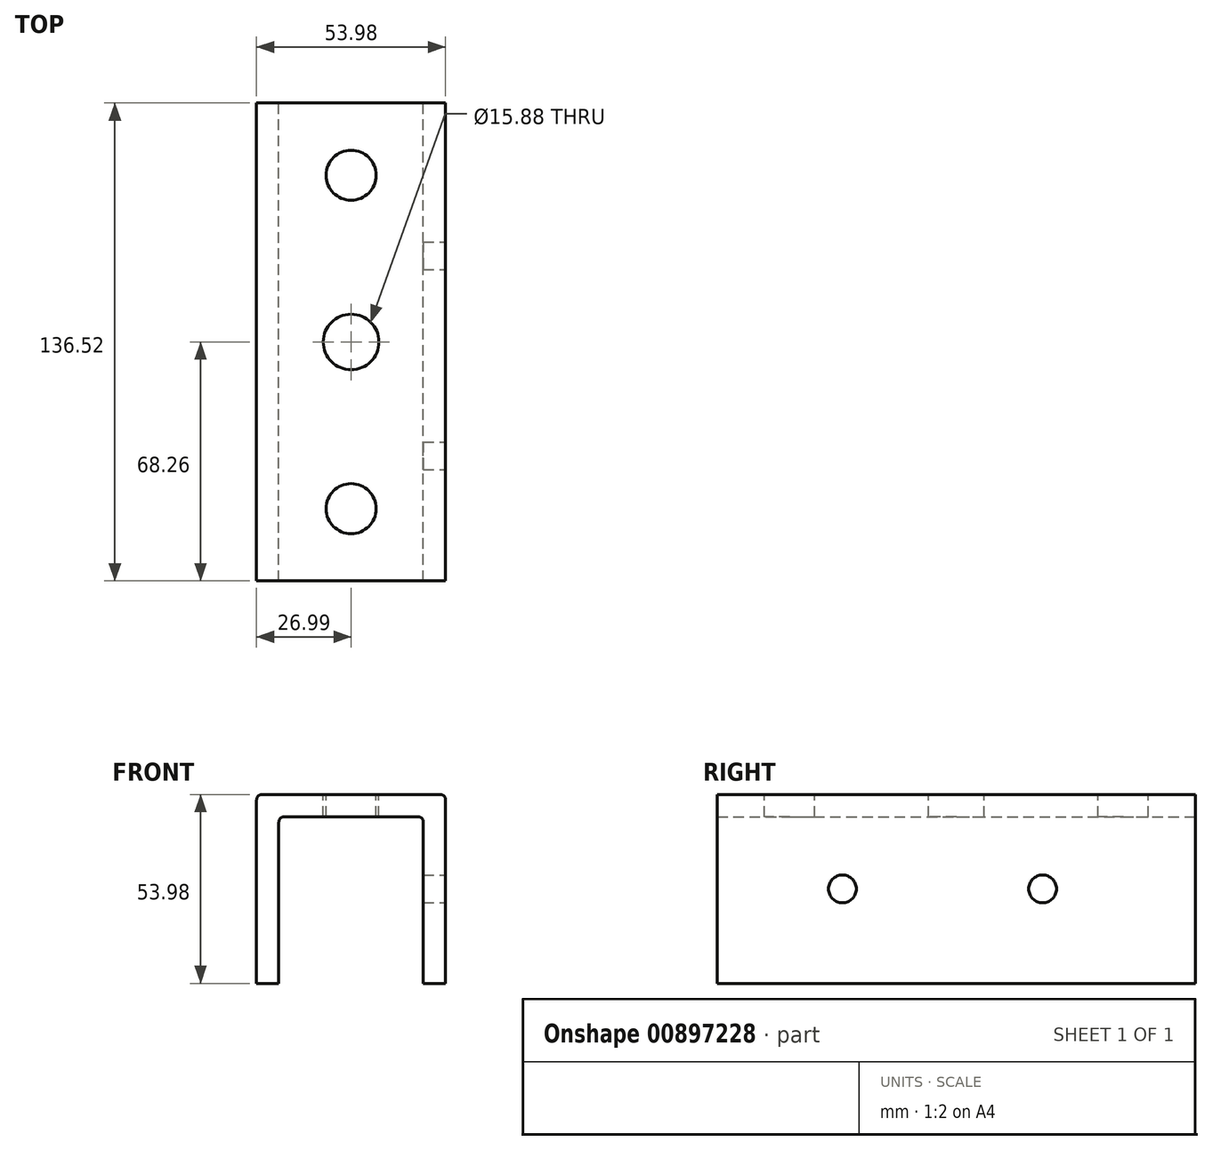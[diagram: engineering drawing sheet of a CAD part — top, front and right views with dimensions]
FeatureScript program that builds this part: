
annotation { "Feature Type Name" : "Feature", "Feature Type Description" : "" }
export const myFeature = defineFeature(function(context is Context, id is Id, definition is map)
    precondition{}
    {
        {
            var Q0;
            Q0=qCreatedBy(makeId("Front.planeOp"),FACE);
            var sketch = newSketch(context, id + "F0", { "sketchPlane" : qUnion([Q0])});
            skLineSegment(sketch, "E0.bottom", {"start": v(19.05, 20.64) * mm, "end": v(-19.05, 20.64) * mm});
            skLineSegment(sketch, "E0.left", {"start": v(20.64, 19.05) * mm, "end": v(20.64, -20.64) * mm});
            skLineSegment(sketch, "E0.right", {"start": v(-20.64, 19.05) * mm, "end": v(-20.64, -20.64) * mm});
            skPoint(sketch, "E0.middle", {"position": v(0, 0) * mm});
            skLineSegment(sketch, "E1.bottom", {"start": v(25.4, 26.99) * mm, "end": v(-25.4, 26.99) * mm});
            skLineSegment(sketch, "E1.top", {"start": v(26.99, -26.99) * mm, "end": v(20.64, -26.99) * mm});
            skLineSegment(sketch, "E1.left", {"start": v(26.99, 25.4) * mm, "end": v(26.99, -26.99) * mm});
            skLineSegment(sketch, "E1.right", {"start": v(-26.99, 25.4) * mm, "end": v(-26.99, -26.99) * mm});
            skLineSegment(sketch, "E2.left", {"start": v(-20.64, -20.64) * mm, "end": v(-20.64, -26.99) * mm});
            skLineSegment(sketch, "E2.right", {"start": v(20.64, -20.64) * mm, "end": v(20.64, -26.99) * mm});
            skLineSegment(sketch, "E3.trimOffspring", {"start": v(-20.64, -26.99) * mm, "end": v(-26.99, -26.99) * mm});
            skPoint(sketch, "E4.visualSharp", {"position": v(-26.99, 26.99) * mm});
            skArc(sketch, "E4.filletArc", {"start": v(-25.4, 26.99) * mm, "mid": v(-26.52, 26.52) * mm, "end": v(-26.99, 25.4) * mm});
            skPoint(sketch, "E5.visualSharp", {"position": v(20.64, 20.64) * mm});
            skArc(sketch, "E5.filletArc", {"start": v(20.64, 19.05) * mm, "mid": v(20.17, 20.17) * mm, "end": v(19.05, 20.64) * mm});
            skPoint(sketch, "E6.visualSharp", {"position": v(-20.64, 20.64) * mm});
            skArc(sketch, "E6.filletArc", {"start": v(-19.05, 20.64) * mm, "mid": v(-20.17, 20.17) * mm, "end": v(-20.64, 19.05) * mm});
            skPoint(sketch, "E7.visualSharp", {"position": v(26.99, 26.99) * mm});
            skArc(sketch, "E7.filletArc", {"start": v(26.99, 25.4) * mm, "mid": v(26.52, 26.52) * mm, "end": v(25.4, 26.99) * mm});
            skSolve(sketch);
        }
        {
            var Q0;
            Q0 = qSketchRegion(id + "F0", true);
            extrude(context, id + "F1", {"entities" : qUnion([Q0]), "endBound" : BoundingType.SYMMETRIC, "depth" : 136.53 * mm, "offsetDistance" : 25.4 * mm});
        }
        {
            var Q0;
            Q0=makeQuery(id+"F1.opExtrude","SWEPT_FACE",FACE,{"disambiguationData":[OSD([sQuery(id+"F0.wireOp",EDGE,"E1.bottom")])]});
            var sketch = newSketch(context, id + "F2", { "sketchPlane" : qUnion([Q0])});
            skCircle(sketch, "E8", {"center": v(0, 0) * mm, "radius": 7.94 * mm});
            skCircle(sketch, "E9", {"center": v(0, 47.63) * mm, "radius": 7.14 * mm});
            skCircle(sketch, "E10", {"center": v(0, -47.63) * mm, "radius": 7.15 * mm});
            skSolve(sketch);
        }
        {
            var Q0;
            Q0 = qSketchRegion(id + "F2", true);
            extrude(context, id + "F3", {"entities" : qUnion([Q0]), "operationType" : NewBodyOperationType.REMOVE, "oppositeDirection" : true, "depth" : 25.4 * mm, "offsetDistance" : 25.4 * mm});
        }
        {
            var Q0;
            Q0=makeQuery(id+"F1.opExtrude","SWEPT_FACE",FACE,{"disambiguationData":[OSD([sQuery(id+"F0.wireOp",EDGE,"E1.left")])]});
            var sketch = newSketch(context, id + "F4", { "sketchPlane" : qUnion([Q0])});
            skCircle(sketch, "E11", {"center": v(-32.54, 0) * mm, "radius": 3.97 * mm});
            skCircle(sketch, "E12", {"center": v(24.6, 0) * mm, "radius": 3.97 * mm});
            skLineSegment(sketch, "E13", {"start": v(0, 0) * mm, "end": v(0, 25.4) * mm, "construction": true});
            skSolve(sketch);
        }
        {
            var Q0;
            Q0 = qSketchRegion(id + "F4", true);
            extrude(context, id + "F5", {"entities" : qUnion([Q0]), "operationType" : NewBodyOperationType.REMOVE, "oppositeDirection" : true, "depth" : 25.4 * mm, "offsetDistance" : 25.4 * mm});
        }
    });
